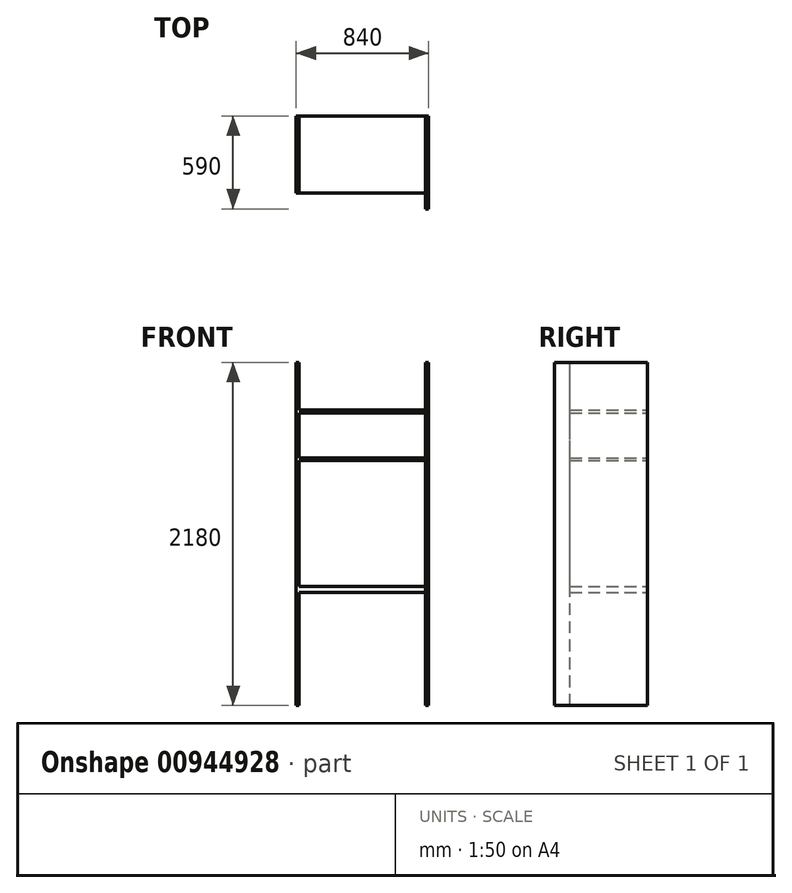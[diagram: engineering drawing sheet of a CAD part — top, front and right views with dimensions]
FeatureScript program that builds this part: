
annotation { "Feature Type Name" : "Feature", "Feature Type Description" : "" }
export const myFeature = defineFeature(function(context is Context, id is Id, definition is map)
    precondition{}
    {
        {
            var Q0;
            Q0=qCreatedBy(makeId("Front.planeOp"),FACE);
            var sketch = newSketch(context, id + "F0", { "sketchPlane" : qUnion([Q0])});
            skLineSegment(sketch, "E0.bottom", {"start": v(0, 0) * mm, "end": v(18, 0) * mm});
            skLineSegment(sketch, "E0.left", {"start": v(0, 0) * mm, "end": v(0, 2180) * mm});
            skLineSegment(sketch, "E0.right", {"start": v(840, 0) * mm, "end": v(840, 2180) * mm});
            skLineSegment(sketch, "E1.0", {"start": v(822, 0) * mm, "end": v(822, 720) * mm});
            skLineSegment(sketch, "E1.2", {"start": v(18, 0) * mm, "end": v(18, 720) * mm});
            skLineSegment(sketch, "E2.trimOffspring", {"start": v(822, 0) * mm, "end": v(840, 0) * mm});
            skLineSegment(sketch, "E3.bottom", {"start": v(18, 720) * mm, "end": v(822, 720) * mm});
            skLineSegment(sketch, "E3.top", {"start": v(18, 756) * mm, "end": v(822, 756) * mm});
            skLineSegment(sketch, "E4.bottom", {"start": v(18, 1859) * mm, "end": v(822, 1859) * mm});
            skLineSegment(sketch, "E4.top", {"start": v(18, 1877) * mm, "end": v(822, 1877) * mm});
            skLineSegment(sketch, "E5.bottom", {"start": v(18, 1556) * mm, "end": v(822, 1556) * mm});
            skLineSegment(sketch, "E5.top", {"start": v(18, 1574) * mm, "end": v(822, 1574) * mm});
            skLineSegment(sketch, "E6.trimOffspring", {"start": v(18, 1877) * mm, "end": v(18, 2162) * mm});
            skLineSegment(sketch, "E7.trimOffspring", {"start": v(822, 1877) * mm, "end": v(822, 2162) * mm});
            skLineSegment(sketch, "E8.trimOffspring", {"start": v(822, 1574) * mm, "end": v(822, 1859) * mm});
            skLineSegment(sketch, "E9.trimOffspring", {"start": v(18, 1574) * mm, "end": v(18, 1859) * mm});
            skLineSegment(sketch, "E10.trimOffspring", {"start": v(18, 756) * mm, "end": v(18, 1556) * mm});
            skLineSegment(sketch, "E11.trimOffspring", {"start": v(822, 756) * mm, "end": v(822, 1556) * mm});
            skLineSegment(sketch, "E12", {"start": v(0, 2180) * mm, "end": v(18, 2180) * mm});
            skLineSegment(sketch, "E13", {"start": v(18, 2180) * mm, "end": v(18, 2162) * mm});
            skLineSegment(sketch, "E14", {"start": v(822, 2162) * mm, "end": v(822, 2180) * mm});
            skLineSegment(sketch, "E15", {"start": v(822, 2180) * mm, "end": v(840, 2180) * mm});
            skSolve(sketch);
        }
        {
            var Q0;
            Q0 = qSketchRegion(id + "F0", true);
            extrude(context, id + "F1", {"entities" : qUnion([Q0]), "depth" : 490 * mm, "offsetDistance" : 25 * mm});
        }
        {
            var Q0;
            Q0=makeQuery(id+"F1.opExtrude","SWEPT_FACE",FACE,{"disambiguationData":[OSD([sQuery(id+"F0.wireOp",EDGE,"E0.right")])]});
            var sketch = newSketch(context, id + "F2", { "sketchPlane" : qUnion([Q0])});
            skLineSegment(sketch, "E16.bottom", {"start": v(-490, 2180) * mm, "end": v(-590, 2180) * mm});
            skLineSegment(sketch, "E16.top", {"start": v(-490, 0) * mm, "end": v(-590, 0) * mm});
            skLineSegment(sketch, "E16.left", {"start": v(-490, 2180) * mm, "end": v(-490, 0) * mm});
            skLineSegment(sketch, "E16.right", {"start": v(-590, 2180) * mm, "end": v(-590, 0) * mm});
            skSolve(sketch);
        }
        {
            var Q0;
            Q0 = qSketchRegion(id + "F2", true);
            extrude(context, id + "F3", {"entities" : qUnion([Q0]), "operationType" : NewBodyOperationType.ADD, "oppositeDirection" : true, "depth" : 18 * mm, "offsetDistance" : 25 * mm});
        }
    });
